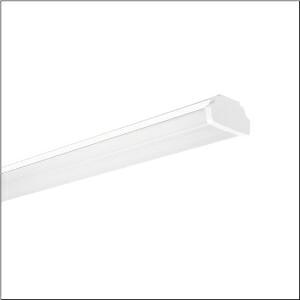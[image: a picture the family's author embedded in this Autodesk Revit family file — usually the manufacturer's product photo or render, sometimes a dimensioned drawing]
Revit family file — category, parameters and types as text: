
# Revit family: modario_r__31_mo_53bm81271v4080_0fb4
name_source: partatom
category: Lighting Fixtures
units: mm (PartAtom-declared; Revit-internal decimal feet)

## family parameters
Cut with Voids When Loaded = No
Host = Face
Light Source = No
Part Type = Normal
Room Calculation Point = No
Round Connector Dimension = Use Diameter
Shared = No

## types (1)
- Modario® 31 MO (1 x LED, 7810 lm, 50.8 W, 4000K)
    Apparent Load = 51 VA
    CIE Flux Codes = 47 80 95 92 100
    Color Rendering = 80
    Color Temperature = 4000K
    Default Elevation = 1800 mm
    Description = Modario® 31 MO, luminaire insert, of sheet steel, coil coated, white, length: 1.495mm, width: 81mm, height: 82mm, 5x system unit, system units: 299mm, LED rated luminous flux: 7.810lm, light colour: 840, control gear: ON/OFF, control gear: ECG, with plug, 3-pole, with phase selection, mains connection: 220..240V, AC, 50/60Hz, rated input power: 51W, through-wiring accessed according to module size, primary optical cover: cover, of PMMA, light emission: direct distribution, primary light characteristic: symmetric, protection rating (complete): IP20, protection rating (LED compartment): IP50, insulation class (complete): insulation class I (protective earthing), certification: CE, ENEC, VDE, UKCA, impact resistance: IK03, permissible ambient temperature for indoor applications: -35..+35°C, corresponds to IFS (International Featured Standards) requirements for safety and quality in the food industry, reducing of maximum allowable ambient temperature of 5°C with ceiling mounting, packaging unit: 1 piece
    Height = 92 mm
    Lamp = 1 x LED
    Lamp Light Flux = 7810 lm
    Lamp Power = 50.8 W
    Lamp count = 1
    Length = 1495 mm
    Luminous efficacy = 154 lm/W
    Manufacturer = Siteco
    ModVariant = No
    Model = 53BM81271V4080
    Mounting Place = Ceiling
    Mounting Type = Pendant
    Number of Poles = 1
    OnlyDefault = Yes
    Power Factor = 1
    Product Name = Modario® 31 MO
    Product group = luminaire insert
    ProductGroupID = 901
    Protection Class = Protection class I
    Protection Degree = IP 20
    RLX_Detail_Level = 1
    RLX_Emergency_Light_Flux = 0 lm
    RLX_Emergency_Type = 0
    RLX_Emergency_Type_DB = No
    RlxData = <blob elided: 38669 chars, md5=dfc044e6>
    Socket = socket
    Standby Power = 0 W
    System Light Flux = 7810 lm
    System Power = 51 W
    Type Comments = Product without accessories
    Type Image = l_1300283.jpg
    URL = http://relux.com
    VarID = ---
    Voltage = 0 V
    Weight = 0.00 kg
    Width = 81 mm

## geometry (parser evidence)
native form markers: Blend x4, Sweep x13
no freeform markers — native parametric forms only
